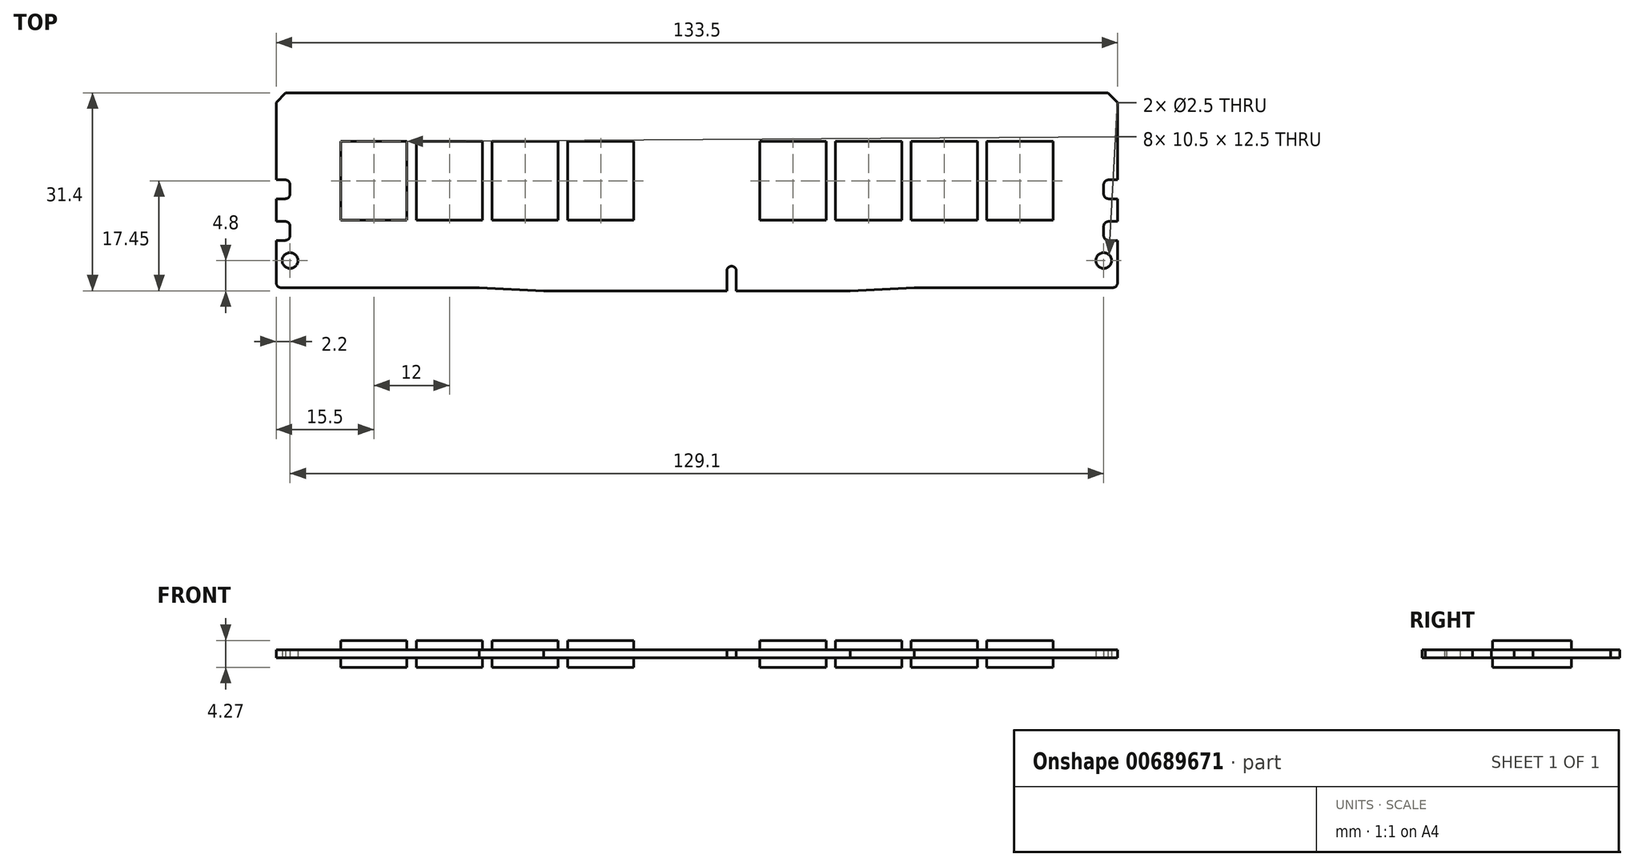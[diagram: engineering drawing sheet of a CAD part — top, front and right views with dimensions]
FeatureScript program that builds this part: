
annotation { "Feature Type Name" : "Feature", "Feature Type Description" : "" }
export const myFeature = defineFeature(function(context is Context, id is Id, definition is map)
    precondition{}
    {
        {
            var Q0;
            Q0=qCreatedBy(makeId("Top.planeOp"),FACE);
            var sketch = newSketch(context, id + "F0", { "sketchPlane" : qUnion([Q0])});
            skLineSegment(sketch, "E0.bottom", {"start": v(-66, -15.2) * mm, "end": v(-34.5, -15.2) * mm});
            skLineSegment(sketch, "E0.top", {"start": v(-65.25, 15.7) * mm, "end": v(65.25, 15.7) * mm});
            skLineSegment(sketch, "E0.left", {"start": v(-66.75, -14.45) * mm, "end": v(-66.75, -7.7) * mm});
            skLineSegment(sketch, "E1", {"start": v(-66.75, 14.2) * mm, "end": v(-65.25, 15.7) * mm});
            skPoint(sketch, "E2.orphan", {"position": v(-66.75, 15.7) * mm});
            skLineSegment(sketch, "E3.bottom", {"start": v(-66.75, -1.1) * mm, "end": v(-65.3, -1.1) * mm});
            skLineSegment(sketch, "E3.top", {"start": v(-66.75, 1.9) * mm, "end": v(-65.3, 1.9) * mm});
            skLineSegment(sketch, "E3.right", {"start": v(-64.55, -0.35) * mm, "end": v(-64.55, 1.15) * mm});
            skLineSegment(sketch, "E4.trimOffspring", {"start": v(-66.75, 1.9) * mm, "end": v(-66.75, 14.2) * mm});
            skPoint(sketch, "E5.visualSharp", {"position": v(-64.55, -1.1) * mm});
            skArc(sketch, "E5.filletArc", {"start": v(-65.3, -1.1) * mm, "mid": v(-64.77, -0.88) * mm, "end": v(-64.55, -0.35) * mm});
            skPoint(sketch, "E6.visualSharp", {"position": v(-64.55, 1.9) * mm});
            skArc(sketch, "E6.filletArc", {"start": v(-64.55, 1.15) * mm, "mid": v(-64.77, 1.68) * mm, "end": v(-65.3, 1.9) * mm});
            skLineSegment(sketch, "E7.bottom", {"start": v(-66.75, -7.7) * mm, "end": v(-65.3, -7.7) * mm});
            skLineSegment(sketch, "E7.top", {"start": v(-66.75, -4.7) * mm, "end": v(-65.3, -4.7) * mm});
            skLineSegment(sketch, "E7.right", {"start": v(-64.55, -6.95) * mm, "end": v(-64.55, -5.45) * mm});
            skPoint(sketch, "E8.visualSharp", {"position": v(-64.55, -7.7) * mm});
            skArc(sketch, "E8.filletArc", {"start": v(-65.3, -7.7) * mm, "mid": v(-64.77, -7.48) * mm, "end": v(-64.55, -6.95) * mm});
            skPoint(sketch, "E9.visualSharp", {"position": v(-64.55, -4.7) * mm});
            skArc(sketch, "E9.filletArc", {"start": v(-64.55, -5.45) * mm, "mid": v(-64.77, -4.92) * mm, "end": v(-65.3, -4.7) * mm});
            skCircle(sketch, "E10", {"center": v(-64.55, -10.9) * mm, "radius": 1.25 * mm});
            skLineSegment(sketch, "E11", {"start": v(-34.5, -15.2) * mm, "end": v(-24.3, -15.7) * mm});
            skLineSegment(sketch, "E12", {"start": v(-24.3, -15.7) * mm, "end": v(4.75, -15.7) * mm});
            skLineSegment(sketch, "E13", {"start": v(24.3, -15.7) * mm, "end": v(34.5, -15.2) * mm});
            skLineSegment(sketch, "E14.trimOffspring", {"start": v(34.5, -15.2) * mm, "end": v(66, -15.2) * mm});
            skPoint(sketch, "E15.visualSharp", {"position": v(-66.75, -15.2) * mm});
            skArc(sketch, "E15.filletArc", {"start": v(-66.75, -14.45) * mm, "mid": v(-66.53, -14.98) * mm, "end": v(-66, -15.2) * mm});
            skLineSegment(sketch, "E16.trimOffspring", {"start": v(-66.75, -4.7) * mm, "end": v(-66.75, -1.1) * mm});
            skArc(sketch, "E17.MirrorCS", {"start": v(64.55, 1.15) * mm, "mid": v(64.77, 1.68) * mm, "end": v(65.3, 1.9) * mm});
            skArc(sketch, "E18.MirrorCS", {"start": v(65.3, -1.1) * mm, "mid": v(64.77, -0.88) * mm, "end": v(64.55, -0.35) * mm});
            skArc(sketch, "E19.MirrorCS", {"start": v(65.3, -7.7) * mm, "mid": v(64.77, -7.48) * mm, "end": v(64.55, -6.95) * mm});
            skArc(sketch, "E20.MirrorCS", {"start": v(64.55, -5.45) * mm, "mid": v(64.77, -4.92) * mm, "end": v(65.3, -4.7) * mm});
            skPoint(sketch, "E21.MirrorP", {"position": v(64.55, -7.7) * mm});
            skLineSegment(sketch, "E22.MirrorCS", {"start": v(66.75, -7.7) * mm, "end": v(65.3, -7.7) * mm});
            skPoint(sketch, "E23.MirrorP", {"position": v(64.55, 1.9) * mm});
            skPoint(sketch, "E24.MirrorP", {"position": v(64.55, -4.7) * mm});
            skLineSegment(sketch, "E25.MirrorCS", {"start": v(66.75, -4.7) * mm, "end": v(65.3, -4.7) * mm});
            skPoint(sketch, "E26.MirrorP", {"position": v(64.55, -1.1) * mm});
            skLineSegment(sketch, "E27.MirrorCS", {"start": v(64.55, -0.35) * mm, "end": v(64.55, 1.15) * mm});
            skLineSegment(sketch, "E28.MirrorCS", {"start": v(66.75, -1.1) * mm, "end": v(65.3, -1.1) * mm});
            skCircle(sketch, "E29.MirrorC", {"center": v(64.55, -10.9) * mm, "radius": 1.25 * mm});
            skLineSegment(sketch, "E30.MirrorCS", {"start": v(66.75, 1.9) * mm, "end": v(65.3, 1.9) * mm});
            skLineSegment(sketch, "E31.MirrorCS", {"start": v(66.75, -4.7) * mm, "end": v(66.75, -1.1) * mm});
            skLineSegment(sketch, "E32.MirrorCS", {"start": v(64.55, -6.95) * mm, "end": v(64.55, -5.45) * mm});
            skLineSegment(sketch, "E33.trimOffspring", {"start": v(66.75, 1.9) * mm, "end": v(66.75, 14.2) * mm});
            skLineSegment(sketch, "E34", {"start": v(66.75, 14.2) * mm, "end": v(65.25, 15.7) * mm});
            skLineSegment(sketch, "E35", {"start": v(66.75, -14.45) * mm, "end": v(66.75, -7.7) * mm});
            skPoint(sketch, "E36.visualSharp", {"position": v(66.75, -15.2) * mm});
            skArc(sketch, "E36.filletArc", {"start": v(66, -15.2) * mm, "mid": v(66.53, -14.98) * mm, "end": v(66.75, -14.45) * mm});
            skLineSegment(sketch, "E37.top", {"start": v(5.5, -11.8) * mm, "end": v(5.5, -11.8) * mm});
            skLineSegment(sketch, "E37.left", {"start": v(4.75, -15.7) * mm, "end": v(4.75, -12.55) * mm});
            skLineSegment(sketch, "E37.right", {"start": v(6.25, -15.7) * mm, "end": v(6.25, -12.55) * mm});
            skPoint(sketch, "E38.visualSharp", {"position": v(4.75, -11.8) * mm});
            skArc(sketch, "E38.filletArc", {"start": v(5.5, -11.8) * mm, "mid": v(4.97, -12.02) * mm, "end": v(4.75, -12.55) * mm});
            skPoint(sketch, "E39.visualSharp", {"position": v(6.25, -11.8) * mm});
            skArc(sketch, "E39.filletArc", {"start": v(6.25, -12.55) * mm, "mid": v(6.03, -12.02) * mm, "end": v(5.5, -11.8) * mm});
            skLineSegment(sketch, "E40.trimOffspring", {"start": v(6.25, -15.7) * mm, "end": v(24.3, -15.7) * mm});
            skSolve(sketch);
        }
        {
            var Q0;
            Q0 = qSketchRegion(id + "F0", true);
            extrude(context, id + "F1", {"entities" : qUnion([Q0]), "depth" : 1.27 * mm, "offsetDistance" : 25 * mm});
        }
        {
            var Q0;
            Q0=makeQuery(id+"F1.opExtrude","CAP_FACE",FACE,{"disambiguationData":[OSD([sQuery(id+"F0.wireOp",EDGE,"E0.bottom"),sQuery(id+"F0.wireOp",EDGE,"E0.top"),sQuery(id+"F0.wireOp",EDGE,"E0.left"),sQuery(id+"F0.wireOp",EDGE,"E1"),sQuery(id+"F0.wireOp",EDGE,"E3.bottom"),sQuery(id+"F0.wireOp",EDGE,"E3.top"),sQuery(id+"F0.wireOp",EDGE,"E3.right"),sQuery(id+"F0.wireOp",EDGE,"E4.trimOffspring"),sQuery(id+"F0.wireOp",EDGE,"E5.filletArc"),sQuery(id+"F0.wireOp",EDGE,"E6.filletArc"),sQuery(id+"F0.wireOp",EDGE,"E7.bottom"),sQuery(id+"F0.wireOp",EDGE,"E7.top"),sQuery(id+"F0.wireOp",EDGE,"E7.right"),sQuery(id+"F0.wireOp",EDGE,"E8.filletArc"),sQuery(id+"F0.wireOp",EDGE,"E9.filletArc"),sQuery(id+"F0.wireOp",EDGE,"E10"),sQuery(id+"F0.wireOp",EDGE,"E11"),sQuery(id+"F0.wireOp",EDGE,"E12"),sQuery(id+"F0.wireOp",EDGE,"E13"),sQuery(id+"F0.wireOp",EDGE,"E14.trimOffspring"),sQuery(id+"F0.wireOp",EDGE,"E15.filletArc"),sQuery(id+"F0.wireOp",EDGE,"E16.trimOffspring"),sQuery(id+"F0.wireOp",EDGE,"E17.MirrorCS"),sQuery(id+"F0.wireOp",EDGE,"E18.MirrorCS"),sQuery(id+"F0.wireOp",EDGE,"E19.MirrorCS"),sQuery(id+"F0.wireOp",EDGE,"E20.MirrorCS"),sQuery(id+"F0.wireOp",EDGE,"E22.MirrorCS"),sQuery(id+"F0.wireOp",EDGE,"E25.MirrorCS"),sQuery(id+"F0.wireOp",EDGE,"E27.MirrorCS"),sQuery(id+"F0.wireOp",EDGE,"E28.MirrorCS"),sQuery(id+"F0.wireOp",EDGE,"E29.MirrorC"),sQuery(id+"F0.wireOp",EDGE,"E30.MirrorCS"),sQuery(id+"F0.wireOp",EDGE,"E32.MirrorCS"),sQuery(id+"F0.wireOp",EDGE,"E31.MirrorCS"),sQuery(id+"F0.wireOp",EDGE,"E33.trimOffspring"),sQuery(id+"F0.wireOp",EDGE,"E34"),sQuery(id+"F0.wireOp",EDGE,"E35"),sQuery(id+"F0.wireOp",EDGE,"E36.filletArc"),sQuery(id+"F0.wireOp",EDGE,"E37.left"),sQuery(id+"F0.wireOp",EDGE,"E37.right"),sQuery(id+"F0.wireOp",EDGE,"E38.filletArc"),sQuery(id+"F0.wireOp",EDGE,"E39.filletArc"),sQuery(id+"F0.wireOp",EDGE,"E40.trimOffspring")])],"isStart":false});
            var sketch = newSketch(context, id + "F2", { "sketchPlane" : qUnion([Q0])});
            skLineSegment(sketch, "E41.bottom", {"start": v(-56.5, 8) * mm, "end": v(-46, 8) * mm});
            skLineSegment(sketch, "E41.top", {"start": v(-56.5, -4.5) * mm, "end": v(-46, -4.5) * mm});
            skLineSegment(sketch, "E41.left", {"start": v(-56.5, 8) * mm, "end": v(-56.5, -4.5) * mm});
            skLineSegment(sketch, "E41.right", {"start": v(-46, 8) * mm, "end": v(-46, -4.5) * mm});
            skLineSegment(sketch, "E42.1.0.1", {"start": v(-44.5, 8) * mm, "end": v(-44.5, -4.5) * mm});
            skLineSegment(sketch, "E42.1.0.2", {"start": v(-34, 8) * mm, "end": v(-34, -4.5) * mm});
            skLineSegment(sketch, "E42.1.0.3", {"start": v(-44.5, 8) * mm, "end": v(-34, 8) * mm});
            skLineSegment(sketch, "E42.2.0.0", {"start": v(-32.5, -4.5) * mm, "end": v(-22, -4.5) * mm});
            skLineSegment(sketch, "E42.2.0.1", {"start": v(-32.5, 8) * mm, "end": v(-32.5, -4.5) * mm});
            skLineSegment(sketch, "E42.2.0.2", {"start": v(-22, 8) * mm, "end": v(-22, -4.5) * mm});
            skLineSegment(sketch, "E42.2.0.3", {"start": v(-32.5, 8) * mm, "end": v(-22, 8) * mm});
            skLineSegment(sketch, "E42.3.0.0", {"start": v(-20.5, -4.5) * mm, "end": v(-10, -4.5) * mm});
            skLineSegment(sketch, "E42.3.0.1", {"start": v(-20.5, 8) * mm, "end": v(-20.5, -4.5) * mm});
            skLineSegment(sketch, "E42.3.0.2", {"start": v(-10, 8) * mm, "end": v(-10, -4.5) * mm});
            skLineSegment(sketch, "E42.3.0.3", {"start": v(-20.5, 8) * mm, "end": v(-10, 8) * mm});
            skLineSegment(sketch, "E42.direction1", {"start": v(-56.5, -4.5) * mm, "end": v(-46, -4.5) * mm, "construction": true});
            skLineSegment(sketch, "E43", {"start": v(0, 0) * mm, "end": v(0, 24.2) * mm, "construction": true});
            skPoint(sketch, "E43.endSnap0", {"position": v(0, 15.7) * mm});
            skLineSegment(sketch, "E44.MirrorCS", {"start": v(0, -9) * mm, "end": v(0, -33.2) * mm, "construction": true});
            skLineSegment(sketch, "E45.MirrorCS", {"start": v(56.5, -4.5) * mm, "end": v(46, -4.5) * mm});
            skLineSegment(sketch, "E46.MirrorCS", {"start": v(44.5, -4.5) * mm, "end": v(34, -4.5) * mm});
            skLineSegment(sketch, "E47.MirrorCS", {"start": v(20.5, -4.5) * mm, "end": v(10, -4.5) * mm});
            skLineSegment(sketch, "E48.MirrorCS", {"start": v(32.5, -4.5) * mm, "end": v(22, -4.5) * mm});
            skLineSegment(sketch, "E49.MirrorCS", {"start": v(32.5, 8) * mm, "end": v(32.5, -4.5) * mm});
            skLineSegment(sketch, "E50.MirrorCS", {"start": v(22, -17) * mm, "end": v(22, -4.5) * mm});
            skLineSegment(sketch, "E51.MirrorCS", {"start": v(56.5, -17) * mm, "end": v(56.5, -4.5) * mm});
            skLineSegment(sketch, "E52.MirrorCS", {"start": v(34, 8) * mm, "end": v(34, -4.5) * mm});
            skLineSegment(sketch, "E53.MirrorCS", {"start": v(20.5, -17) * mm, "end": v(20.5, -4.5) * mm});
            skLineSegment(sketch, "E54.MirrorCS", {"start": v(46, -17) * mm, "end": v(46, -4.5) * mm});
            skLineSegment(sketch, "E55.MirrorCS", {"start": v(22, 8) * mm, "end": v(22, -4.5) * mm});
            skLineSegment(sketch, "E56.MirrorCS", {"start": v(44.5, 8) * mm, "end": v(44.5, -4.5) * mm});
            skLineSegment(sketch, "E57.MirrorCS", {"start": v(20.5, 8) * mm, "end": v(20.5, -4.5) * mm});
            skLineSegment(sketch, "E58.MirrorCS", {"start": v(34, -17) * mm, "end": v(34, -4.5) * mm});
            skLineSegment(sketch, "E59.MirrorCS", {"start": v(46, 8) * mm, "end": v(46, -4.5) * mm});
            skLineSegment(sketch, "E60.MirrorCS", {"start": v(10, -17) * mm, "end": v(10, -4.5) * mm});
            skLineSegment(sketch, "E61.MirrorCS", {"start": v(44.5, -17) * mm, "end": v(44.5, -4.5) * mm});
            skLineSegment(sketch, "E62.MirrorCS", {"start": v(10, 8) * mm, "end": v(10, -4.5) * mm});
            skLineSegment(sketch, "E63.MirrorCS", {"start": v(32.5, -17) * mm, "end": v(32.5, -4.5) * mm});
            skLineSegment(sketch, "E64.MirrorCS", {"start": v(56.5, 8) * mm, "end": v(56.5, -4.5) * mm});
            skLineSegment(sketch, "E65.MirrorCS", {"start": v(56.5, -4.5) * mm, "end": v(44.5, -4.5) * mm, "construction": true});
            skLineSegment(sketch, "E66.MirrorCS", {"start": v(20.5, 8) * mm, "end": v(10, 8) * mm});
            skLineSegment(sketch, "E67.MirrorCS", {"start": v(56.5, 8) * mm, "end": v(46, 8) * mm});
            skLineSegment(sketch, "E68.MirrorCS", {"start": v(32.5, 8) * mm, "end": v(22, 8) * mm});
            skLineSegment(sketch, "E69.MirrorCS", {"start": v(44.5, 8) * mm, "end": v(34, 8) * mm});
            skPoint(sketch, "E70.MirrorCS.start.orphan", {"position": v(-22, -17) * mm});
            skPoint(sketch, "E71.MirrorCS.start.orphan", {"position": v(-20.5, -17) * mm});
            skPoint(sketch, "E72.MirrorCS.start.orphan", {"position": v(-10, -17) * mm});
            skPoint(sketch, "E73.MirrorCS.start.orphan", {"position": v(-56.5, -17) * mm});
            skLineSegment(sketch, "E74", {"start": v(-44.5, -4.5) * mm, "end": v(-34, -4.5) * mm});
            skSolve(sketch);
        }
        {
            var Q0;
            Q0 = qSketchRegion(id + "F2", true);
            extrude(context, id + "F3", {"entities" : qUnion([Q0]), "operationType" : NewBodyOperationType.ADD, "depth" : 1.5 * mm, "offsetDistance" : 25 * mm});
        }
        {
            var Q0;
            Q0 = qSketchRegion(id + "F2", true);
            extrude(context, id + "F4", {"entities" : qUnion([Q0]), "operationType" : NewBodyOperationType.ADD, "oppositeDirection" : true, "depth" : 2.77 * mm, "offsetDistance" : 25 * mm});
        }
    });
